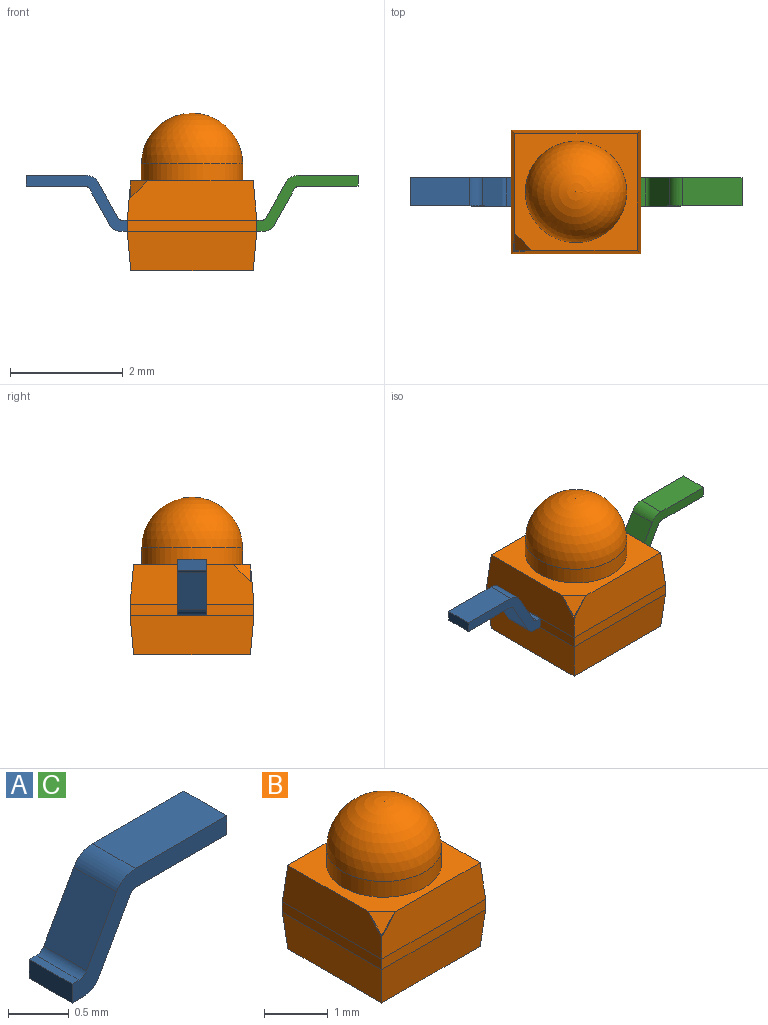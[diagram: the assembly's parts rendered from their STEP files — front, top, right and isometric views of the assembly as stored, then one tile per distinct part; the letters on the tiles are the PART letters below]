
ASSEMBLY  parts=3 mates=2
PART A: 14 faces, bbox 1.8x0.5x1 mm
  f0: plane 0.5x0.19mm, normal (-1,0,0), area 0.1mm2, adj f1,f7,f8,f9
  f1: plane 0.5x0.13mm, normal (0,0,-1), area 0.1mm2, adj f0,f8,f9,f10
  f2: plane 0.65x0.5mm, normal (0.87,0,-0.49), area 0.4mm2, adj f8,f9,f10,f13
  f3: plane 1.04x0.5mm, normal (0,0,-1), area 0.5mm2, adj f4,f8,f9,f13
  f4: plane 0.5x0.19mm, normal (1,0,0), area 0.1mm2, adj f3,f5,f8,f9
  f5: plane 1.07x0.5mm, normal (0,0,1), area 0.5mm2, adj f4,f8,f9,f12
  f6: plane 0.62x0.5mm, normal (-0.87,0,0.49), area 0.4mm2, adj f8,f9,f11,f12
  f7: plane 0.5x0.08mm, normal (0,0,1), area 0mm2, adj f0,f8,f9,f11
  f8: plane 1.8x0.99mm, normal (0,-1,0), area 0.4mm2, adj f0,f1,f2,f3,f4,f5,f6,f7
  f9: plane 1.8x0.99mm, normal (0,1,0), area 0.4mm2, adj f0,f1,f2,f3,f4,f5,f6,f7
  f10: cylinder r=0.2mm len=0.5mm, axis (0,1,0), area 0.1mm2, adj f1,f2,f8,f9
  f11: cylinder r=0.1mm len=0.5mm, axis (0,-1,0), area 0.1mm2, adj f6,f7,f8,f9
  f12: cylinder r=0.25mm len=0.5mm, axis (0,1,0), area 0.1mm2, adj f5,f6,f8,f9
  f13: cylinder r=0.1mm len=0.5mm, axis (0,-1,0), area 0.1mm2, adj f2,f3,f8,f9
PART B: 20 faces, bbox 2.3x2.2x2.8 mm
  f0: plane 2.3x0.7mm, normal (0,-1,0.09), area 1.5mm2, adj f6,f8,f13,f15,f16,f17
  f1: cylinder r=0.9mm len=1.8mm, axis (0,0,1), area 1.7mm2, adj f2,f8
  f2: sphere r=0.9mm, area 5.1mm2, adj f1
  f3: plane 2.2x0.2mm, normal (-1,0,0), area 0.4mm2, adj f4,f6,f10,f13
  f4: plane 2.3x0.2mm, normal (0,1,0), area 0.5mm2, adj f3,f5,f12,f14
  f5: plane 2.2x0.2mm, normal (1,0,0), area 0.4mm2, adj f4,f6,f11,f15
  f6: plane 2.3x0.2mm, normal (0,-1,0), area 0.5mm2, adj f0,f3,f5,f9
  f7: plane 2.18x2.08mm, normal (0,0,-1), area 4.5mm2, adj f9,f10,f11,f12
  f8: plane 2.18x2.08mm, normal (0,0,1), area 1.9mm2, adj f0,f1,f13,f14,f15,f18
  f9: plane 2.3x0.7mm, normal (0,-1,-0.09), area 1.6mm2, adj f6,f7,f10,f11
  f10: plane 2.2x0.7mm, normal (-1,0,-0.09), area 1.5mm2, adj f3,f7,f9,f12
  f11: plane 2.2x0.7mm, normal (1,0,-0.09), area 1.5mm2, adj f5,f7,f9,f12
  f12: plane 2.3x0.7mm, normal (0,1,-0.09), area 1.6mm2, adj f4,f7,f10,f11
  f13: plane 2.2x0.7mm, normal (-1,0,0.09), area 1.5mm2, adj f0,f3,f8,f14,f16,f19
  f14: plane 2.3x0.7mm, normal (0,1,0.09), area 1.6mm2, adj f4,f8,f13,f15
  f15: plane 2.2x0.7mm, normal (1,0,0.09), area 1.5mm2, adj f0,f5,f8,f14
  f16: plane 0.03x0.03mm, normal (0,0,1), area 0mm2, adj f0,f13,f17,f19
  f17: plane 0.3x0.3mm, normal (-0.71,0,0.71), area 0mm2, adj f0,f16,f18
  f18: plane 0.3x0.3mm, normal (-0.58,-0.58,0.58), area 0.1mm2, adj f8,f17,f19
  f19: plane 0.3x0.3mm, normal (0,-0.71,0.71), area 0mm2, adj f13,f16,f18
PART C: same geometry as A
PLACE A rot(axis=(0,0,1),180deg) t=(-1.15,-0.25,-1.19)mm
PLACE B at identity
PLACE C t=(1.15,0.25,-1.19)mm
MATE planar A.f0 <-> B.f3  axis (1,0,0) through (-1.15,0,-1.1)mm
MATE planar C.f0 <-> B.f5  axis (-1,0,0) through (1.15,0,-1.1)mm
